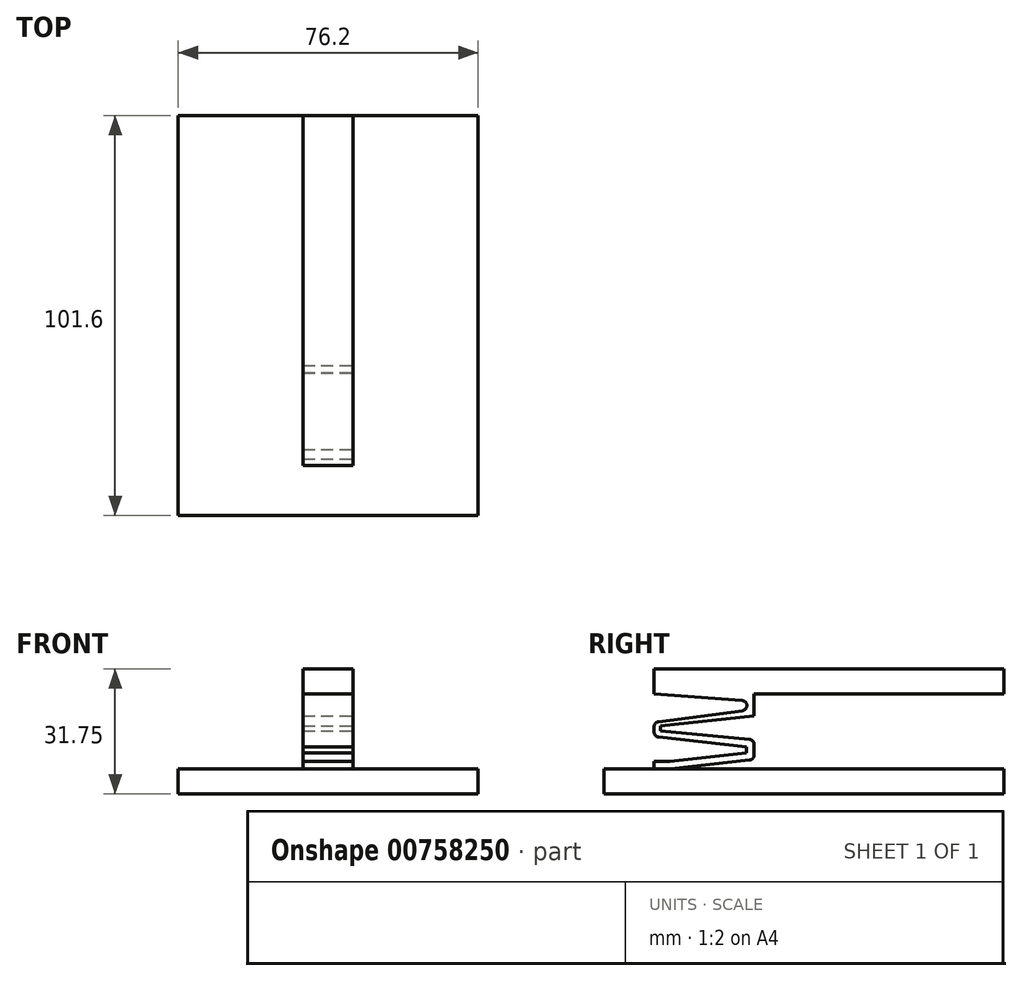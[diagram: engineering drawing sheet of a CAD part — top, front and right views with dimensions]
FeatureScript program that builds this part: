
annotation { "Feature Type Name" : "Feature", "Feature Type Description" : "" }
export const myFeature = defineFeature(function(context is Context, id is Id, definition is map)
    precondition{}
    {
        {
            var Q0;
            Q0=qCreatedBy(makeId("Top.planeOp"),FACE);
            var sketch = newSketch(context, id + "F0", { "sketchPlane" : qUnion([Q0])});
            skLineSegment(sketch, "E0.bottom", {"start": v(-38.1, 50.8) * mm, "end": v(38.1, 50.8) * mm});
            skLineSegment(sketch, "E0.top", {"start": v(-38.1, -50.8) * mm, "end": v(38.1, -50.8) * mm});
            skLineSegment(sketch, "E0.left", {"start": v(-38.1, 50.8) * mm, "end": v(-38.1, -50.8) * mm});
            skLineSegment(sketch, "E0.right", {"start": v(38.1, 50.8) * mm, "end": v(38.1, -50.8) * mm});
            skPoint(sketch, "E1", {"position": v(0, 50.8) * mm});
            skPoint(sketch, "E2", {"position": v(38.1, 0) * mm});
            skSolve(sketch);
        }
        {
            var Q0;
            Q0=makeQuery(id+"F0.imprint","IMPRINT",FACE,{"disambiguationData":[TD([[makeQuery(id+"F0.imprint","IMPRINT",EDGE,{"derivedFrom":sQuery(id+"F0.wireOp",EDGE,"E0.bottom")}),-1.0]])]});
            extrude(context, id + "F1", {"entities" : qUnion([Q0]), "oppositeDirection" : true, "depth" : 6.35 * mm, "offsetDistance" : 25.4 * mm});
        }
        {
            var Q0;
            Q0=makeQuery(id+"F1.opExtrude","CAP_FACE",FACE,{"disambiguationData":[OSD([sQuery(id+"F0.wireOp",EDGE,"E0.bottom"),sQuery(id+"F0.wireOp",EDGE,"E0.top"),sQuery(id+"F0.wireOp",EDGE,"E0.left"),sQuery(id+"F0.wireOp",EDGE,"E0.right")])],"isStart":true});
            var sketch = newSketch(context, id + "F2", { "sketchPlane" : qUnion([Q0])});
            skLineSegment(sketch, "E3.bottom", {"start": v(-6.35, -12.7) * mm, "end": v(6.35, -12.7) * mm});
            skLineSegment(sketch, "E3.top", {"start": v(-6.35, -38.1) * mm, "end": v(6.35, -38.1) * mm});
            skLineSegment(sketch, "E3.left", {"start": v(-6.35, -12.7) * mm, "end": v(-6.35, -38.1) * mm});
            skLineSegment(sketch, "E3.right", {"start": v(6.35, -12.7) * mm, "end": v(6.35, -38.1) * mm});
            skPoint(sketch, "E4", {"position": v(0, -12.7) * mm});
            skSolve(sketch);
        }
        {
            var Q0;
            Q0=makeQuery(id+"F2.imprint","IMPRINT",FACE,{"disambiguationData":[TD([[makeQuery(id+"F2.imprint","IMPRINT",EDGE,{"derivedFrom":sQuery(id+"F2.wireOp",EDGE,"E3.bottom")}),-1.0]])]});
            extrude(context, id + "F3", {"entities" : qUnion([Q0]), "operationType" : NewBodyOperationType.ADD, "depth" : 25.4 * mm, "offsetDistance" : 25.4 * mm});
        }
        {
            var Q0;
            Q0=makeQuery(id+"F3.opExtrude","SWEPT_FACE",FACE,{"disambiguationData":[OSD([sQuery(id+"F2.wireOp",EDGE,"E3.right")])]});
            var sketch = newSketch(context, id + "F4", { "sketchPlane" : qUnion([Q0])});
            skLineSegment(sketch, "E5", {"start": v(-12.7, 25.4) * mm, "end": v(50.8, 25.4) * mm});
            skLineSegment(sketch, "E6", {"start": v(50.8, 25.4) * mm, "end": v(50.8, 19.05) * mm});
            skLineSegment(sketch, "E7", {"start": v(50.8, 19.05) * mm, "end": v(-12.7, 19.05) * mm});
            skSolve(sketch);
        }
        {
            var Q0;
            {var subQ0=sQuery(id+"F4.wireOp",EDGE,"E5");Q0=makeQuery(id+"F4.imprint","IMPRINT",FACE,{"disambiguationData":[TD([[makeQuery(id+"F4.imprint","IMPRINT",EDGE,{"derivedFrom":subQ0}),-1.0]])]});}
            var Q1;
            Q1=makeQuery(id+"F3.opExtrude","SWEPT_FACE",FACE,{"disambiguationData":[OSD([sQuery(id+"F2.wireOp",EDGE,"E3.left")])]});
            extrude(context, id + "F5", {"entities" : qUnion([Q0]), "operationType" : NewBodyOperationType.ADD, "endBound" : BoundingType.UP_TO_SURFACE, "oppositeDirection" : true, "depth" : 25.4 * mm, "endBoundEntityFace" : qUnion([Q1]), "offsetDistance" : 25.4 * mm});
        }
        {
            var Q0;
            {var subQ0=sQuery(id+"F2.wireOp",EDGE,"E3.right");Q0=makeQuery(id+"F5.boolean.opBoolean","MERGE",FACE,{"derivedFrom":[makeQuery(id+"F3.opExtrude","SWEPT_FACE",FACE,{"disambiguationData":[OSD([subQ0])]}),makeQuery(id+"F5.opExtrude","CAP_FACE",FACE,{"disambiguationData":[OSD([sQuery(id+"F2.wireOp",EDGE,"E3.bottom"),subQ0,sQuery(id+"F4.wireOp",EDGE,"E5"),sQuery(id+"F4.wireOp",EDGE,"E6"),sQuery(id+"F4.wireOp",EDGE,"E7")])],"isStart":true})]});}
            var sketch = newSketch(context, id + "F6", { "sketchPlane" : qUnion([Q0])});
            skLineSegment(sketch, "E8", {"start": v(-34.33, 1.86) * mm, "end": v(-38.1, 1.86) * mm});
            skLineSegment(sketch, "E9", {"start": v(-38.1, 0) * mm, "end": v(-34, 0) * mm});
            skLineSegment(sketch, "E10", {"start": v(-34, 0) * mm, "end": v(-12.7, 2.37) * mm});
            skLineSegment(sketch, "E11", {"start": v(-12.7, 2.37) * mm, "end": v(-12.7, 0) * mm});
            skLineSegment(sketch, "E12", {"start": v(-12.7, 0) * mm, "end": v(-34, 0) * mm});
            skLineSegment(sketch, "E13", {"start": v(-34.33, 1.86) * mm, "end": v(-14.62, 4.06) * mm});
            skLineSegment(sketch, "E14", {"start": v(-14.62, 4.06) * mm, "end": v(-14.62, 5.65) * mm});
            skLineSegment(sketch, "E15", {"start": v(-14.62, 5.65) * mm, "end": v(-38.1, 8.22) * mm});
            skLineSegment(sketch, "E16", {"start": v(-12.7, 7.38) * mm, "end": v(-36.42, 9.73) * mm});
            skLineSegment(sketch, "E17", {"start": v(-36.42, 9.73) * mm, "end": v(-36.42, 10.88) * mm});
            skLineSegment(sketch, "E18", {"start": v(-36.42, 10.88) * mm, "end": v(-12.7, 13.48) * mm});
            skLineSegment(sketch, "E19", {"start": v(-14.54, 14.95) * mm, "end": v(-14.54, 17.28) * mm});
            skLineSegment(sketch, "E20", {"start": v(-14.54, 17.28) * mm, "end": v(-38.1, 19.05) * mm});
            skLineSegment(sketch, "E21", {"start": v(-14.54, 14.95) * mm, "end": v(-38.1, 11.85) * mm});
            skLineSegment(sketch, "E22", {"start": v(-38.1, 11.85) * mm, "end": v(-38.1, 19.05) * mm});
            skLineSegment(sketch, "E23", {"start": v(-38.1, 1.86) * mm, "end": v(-38.1, 8.22) * mm});
            skLineSegment(sketch, "E24", {"start": v(-12.7, 13.48) * mm, "end": v(-12.7, 7.38) * mm});
            skLineSegment(sketch, "E25", {"start": v(-12.7, 7.38) * mm, "end": v(-12.7, 2.37) * mm});
            skSolve(sketch);
        }
        {
            var Q0;
            Q0=makeQuery(id+"F6.imprint","IMPRINT",FACE,{"disambiguationData":[TD([[makeQuery(id+"F6.imprint","IMPRINT",EDGE,{"derivedFrom":sQuery(id+"F6.wireOp",EDGE,"E10")}),-1.0]])]});
            var Q1;
            Q1=makeQuery(id+"F6.imprint","IMPRINT",FACE,{"disambiguationData":[TD([[makeQuery(id+"F6.imprint","IMPRINT",EDGE,{"derivedFrom":sQuery(id+"F6.wireOp",EDGE,"E8")}),-1.0]])]});
            var Q2;
            Q2=makeQuery(id+"F6.imprint","IMPRINT",FACE,{"disambiguationData":[TD([[makeQuery(id+"F6.imprint","IMPRINT",EDGE,{"derivedFrom":sQuery(id+"F6.wireOp",EDGE,"E16")}),-1.0]])]});
            var Q3;
            Q3=makeQuery(id+"F6.imprint","IMPRINT",FACE,{"disambiguationData":[TD([[makeQuery(id+"F6.imprint","IMPRINT",EDGE,{"derivedFrom":sQuery(id+"F6.wireOp",EDGE,"E19")}),1.0]])]});
            var Q4;
            {var subQ0=sQuery(id+"F2.wireOp",EDGE,"E3.left");Q4=makeQuery(id+"F5.boolean.opBoolean","MERGE",FACE,{"derivedFrom":[makeQuery(id+"F3.opExtrude","SWEPT_FACE",FACE,{"disambiguationData":[OSD([subQ0])]}),makeQuery(id+"F5.opExtrude","CAP_FACE",FACE,{"disambiguationData":[OSD([subQ0])],"isStart":false})]});}
            extrude(context, id + "F7", {"entities" : qUnion([Q0, Q1, Q2, Q3]), "operationType" : NewBodyOperationType.REMOVE, "endBound" : BoundingType.UP_TO_SURFACE, "oppositeDirection" : true, "depth" : 25.4 * mm, "endBoundEntityFace" : qUnion([Q4]), "offsetDistance" : 25.4 * mm});
        }
        {
            var Q0;
            Q0=makeQuery(id+"F3.opExtrude","CAP_EDGE",EDGE,{"disambiguationData":[OSD([sQuery(id+"F2.wireOp",EDGE,"E3.top")])],"isStart":true});
            var Q1;
            Q1=makeQuery(id+"F7.boolean.opBoolean","COPY",EDGE,{"derivedFrom":makeQuery(id+"F7.opExtrude","SWEPT_EDGE",EDGE,{"disambiguationData":[OSD([sQuery(id+"F6.wireOp",EDGE,"E8"),sQuery(id+"F6.wireOp",EDGE,"E13")])]})});
            fillet(context, id + "F8", {"entities" : qUnion([Q0, Q1]), "radius" : 5.08 * mm, "tangentPropagation" : true, "allowEdgeOverflow" : false});
        }
        {
            var Q0;
            Q0=makeQuery(id+"F7.boolean.opBoolean","COPY",EDGE,{"derivedFrom":makeQuery(id+"F7.opExtrude","SWEPT_EDGE",EDGE,{"disambiguationData":[OSD([sQuery(id+"F6.wireOp",EDGE,"E16"),sQuery(id+"F6.wireOp",EDGE,"E24"),sQuery(id+"F6.wireOp",EDGE,"E25")])]})});
            var Q1;
            Q1=makeQuery(id+"F7.boolean.opBoolean","COPY",EDGE,{"derivedFrom":makeQuery(id+"F7.opExtrude","SWEPT_EDGE",EDGE,{"disambiguationData":[OSD([sQuery(id+"F6.wireOp",EDGE,"E10"),sQuery(id+"F6.wireOp",EDGE,"E11"),sQuery(id+"F6.wireOp",EDGE,"E25")])]})});
            var Q2;
            Q2=makeQuery(id+"F7.boolean.opBoolean","COPY",EDGE,{"derivedFrom":makeQuery(id+"F7.opExtrude","SWEPT_EDGE",EDGE,{"disambiguationData":[OSD([sQuery(id+"F2.wireOp",EDGE,"E3.top"),sQuery(id+"F2.wireOp",EDGE,"E3.right"),sQuery(id+"F6.wireOp",EDGE,"E21"),sQuery(id+"F6.wireOp",EDGE,"E22")])]})});
            var Q3;
            Q3=makeQuery(id+"F7.boolean.opBoolean","COPY",EDGE,{"derivedFrom":makeQuery(id+"F7.opExtrude","SWEPT_EDGE",EDGE,{"disambiguationData":[OSD([sQuery(id+"F2.wireOp",EDGE,"E3.top"),sQuery(id+"F2.wireOp",EDGE,"E3.right"),sQuery(id+"F6.wireOp",EDGE,"E15"),sQuery(id+"F6.wireOp",EDGE,"E23")])]})});
            var Q4;
            Q4=makeQuery(id+"F7.boolean.opBoolean","COPY",EDGE,{"derivedFrom":makeQuery(id+"F7.opExtrude","SWEPT_EDGE",EDGE,{"disambiguationData":[OSD([sQuery(id+"F2.wireOp",EDGE,"E3.bottom"),sQuery(id+"F2.wireOp",EDGE,"E3.right"),sQuery(id+"F6.wireOp",EDGE,"E18"),sQuery(id+"F6.wireOp",EDGE,"E24")])]})});
            var Q5;
            Q5=makeQuery(id+"F7.boolean.opBoolean","COPY",EDGE,{"derivedFrom":makeQuery(id+"F7.opExtrude","SWEPT_EDGE",EDGE,{"disambiguationData":[OSD([sQuery(id+"F2.wireOp",EDGE,"E3.top"),sQuery(id+"F2.wireOp",EDGE,"E3.right"),sQuery(id+"F6.wireOp",EDGE,"E20"),sQuery(id+"F6.wireOp",EDGE,"E22")])]})});
            var Q6;
            Q6=makeQuery(id+"F7.boolean.opBoolean","COPY",EDGE,{"derivedFrom":makeQuery(id+"F7.opExtrude","SWEPT_EDGE",EDGE,{"disambiguationData":[OSD([sQuery(id+"F6.wireOp",EDGE,"E19"),sQuery(id+"F6.wireOp",EDGE,"E20")])]})});
            var Q7;
            Q7=makeQuery(id+"F7.boolean.opBoolean","COPY",EDGE,{"derivedFrom":makeQuery(id+"F7.opExtrude","SWEPT_EDGE",EDGE,{"disambiguationData":[OSD([sQuery(id+"F6.wireOp",EDGE,"E19"),sQuery(id+"F6.wireOp",EDGE,"E21")])]})});
            fillet(context, id + "F9", {"entities" : qUnion([Q0, Q1, Q2, Q3, Q4, Q5, Q6, Q7]), "radius" : 1.27 * mm, "tangentPropagation" : true, "allowEdgeOverflow" : false});
        }
    });
